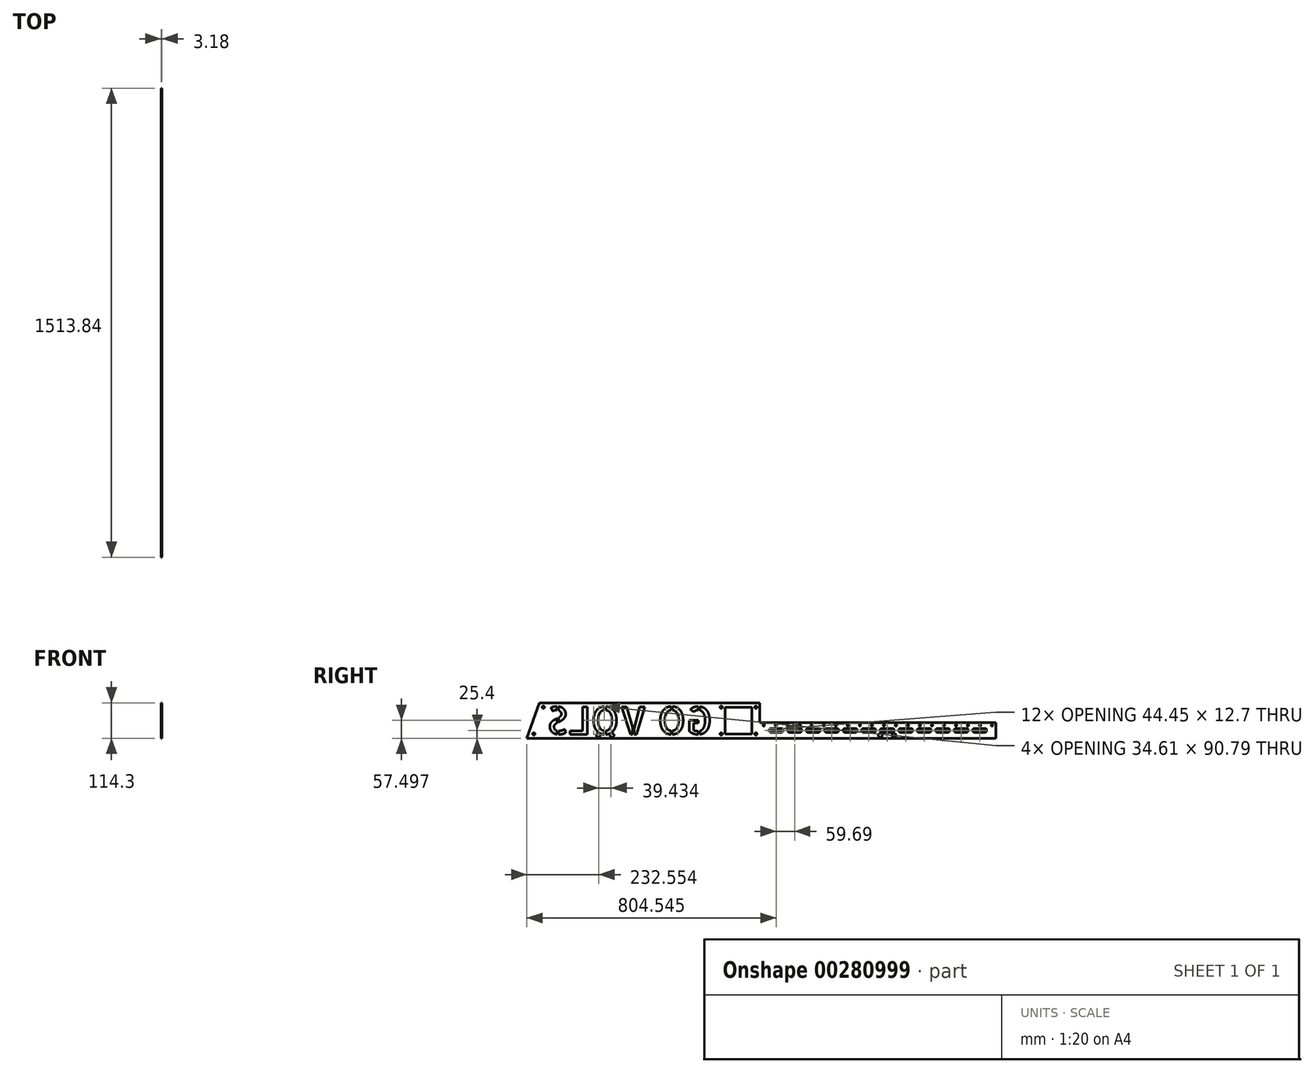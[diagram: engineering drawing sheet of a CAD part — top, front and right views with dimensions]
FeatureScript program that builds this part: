
annotation { "Feature Type Name" : "Feature", "Feature Type Description" : "" }
export const myFeature = defineFeature(function(context is Context, id is Id, definition is map)
    precondition{}
    {
        {
            var Q0;
            Q0=qCreatedBy(makeId("Right.planeOp"),FACE);
            var sketch = newSketch(context, id + "F0", { "sketchPlane" : qUnion([Q0])});
            skLineSegment(sketch, "E0", {"start": v(0, 0) * mm, "end": v(40.64, 114.3) * mm});
            skLineSegment(sketch, "E1", {"start": v(40.64, 114.3) * mm, "end": v(751.84, 114.3) * mm});
            skLineSegment(sketch, "E2", {"start": v(751.84, 114.3) * mm, "end": v(751.84, 50.8) * mm});
            skLineSegment(sketch, "E3", {"start": v(751.84, 50.8) * mm, "end": v(1513.84, 50.8) * mm});
            skLineSegment(sketch, "E4", {"start": v(1513.84, 50.8) * mm, "end": v(1513.84, 0) * mm});
            skLineSegment(sketch, "E5", {"start": v(1513.84, 0) * mm, "end": v(0, 0) * mm});
            skSolve(sketch);
        }
        {
            var Q0;
            Q0=qSketchRegion(id+"F0",true);
            extrude(context, id + "F1", {"entities" : qUnion([Q0]), "oppositeDirection" : true, "depth" : 3.17 * mm});
        }
        {
            var Q0;
            Q0=makeQuery(id+"F1.opExtrude","CAP_FACE",FACE,{"disambiguationData":[OSD([sQuery(id+"F0.wireOp",EDGE,"E0"),sQuery(id+"F0.wireOp",EDGE,"E1"),sQuery(id+"F0.wireOp",EDGE,"E2"),sQuery(id+"F0.wireOp",EDGE,"E3"),sQuery(id+"F0.wireOp",EDGE,"E4"),sQuery(id+"F0.wireOp",EDGE,"E5")])],"isStart":true});
            var sketch = newSketch(context, id + "F2", { "sketchPlane" : qUnion([Q0])});
            skLineSegment(sketch, "E6.bottom", {"start": v(726.44, 13.97) * mm, "end": v(640.08, 13.97) * mm});
            skLineSegment(sketch, "E6.top", {"start": v(726.44, 100.33) * mm, "end": v(640.08, 100.33) * mm});
            skLineSegment(sketch, "E6.left", {"start": v(726.44, 13.97) * mm, "end": v(726.44, 100.33) * mm});
            skLineSegment(sketch, "E6.right", {"start": v(640.08, 13.97) * mm, "end": v(640.08, 100.33) * mm});
            skPoint(sketch, "E6.middle", {"position": v(683.26, 57.15) * mm});
            skSolve(sketch);
        }
        {
            var Q0;
            Q0=qSketchRegion(id+"F2",true);
            var Q1;
            Q1=makeQuery(id+"F1.opExtrude","CAP_FACE",FACE,{"disambiguationData":[OSD([sQuery(id+"F0.wireOp",EDGE,"E0"),sQuery(id+"F0.wireOp",EDGE,"E1"),sQuery(id+"F0.wireOp",EDGE,"E2"),sQuery(id+"F0.wireOp",EDGE,"E3"),sQuery(id+"F0.wireOp",EDGE,"E4"),sQuery(id+"F0.wireOp",EDGE,"E5")])],"isStart":false});
            extrude(context, id + "F3", {"entities" : qUnion([Q0]), "operationType" : NewBodyOperationType.REMOVE, "endBound" : BoundingType.UP_TO_SURFACE, "oppositeDirection" : true, "endBoundEntityFace" : qUnion([Q1]), "depth" : 25.4 * mm});
        }
        {
            var Q0;
            Q0=makeQuery(id+"F1.opExtrude","CAP_FACE",FACE,{"disambiguationData":[OSD([sQuery(id+"F0.wireOp",EDGE,"E0"),sQuery(id+"F0.wireOp",EDGE,"E1"),sQuery(id+"F0.wireOp",EDGE,"E2"),sQuery(id+"F0.wireOp",EDGE,"E3"),sQuery(id+"F0.wireOp",EDGE,"E4"),sQuery(id+"F0.wireOp",EDGE,"E5")])],"isStart":true});
            var sketch = newSketch(context, id + "F4", { "sketchPlane" : qUnion([Q0])});
            skLineSegment(sketch, "E7", {"start": v(683.26, 100.33) * mm, "end": v(683.26, 63.34) * mm, "construction": true});
            skPoint(sketch, "E7.endSnap0", {"position": v(683.26, 100.33) * mm});
            skLineSegment(sketch, "E8", {"start": v(640.08, 57.15) * mm, "end": v(671.5, 57.15) * mm, "construction": true});
            skLineSegment(sketch, "E9", {"start": v(640.08, 100.33) * mm, "end": v(-159.31, 100.33) * mm, "construction": true});
            skCircle(sketch, "E10", {"center": v(739.14, 100.33) * mm, "radius": 3.81 * mm});
            skCircle(sketch, "E11.MirrorC", {"center": v(627.38, 100.33) * mm, "radius": 3.81 * mm});
            skCircle(sketch, "E12.MirrorC", {"center": v(627.38, 13.97) * mm, "radius": 3.81 * mm});
            skCircle(sketch, "E13.MirrorC", {"center": v(739.14, 13.97) * mm, "radius": 3.81 * mm});
            skCircle(sketch, "E14", {"center": v(53.34, 100.33) * mm, "radius": 3.81 * mm});
            skLineSegment(sketch, "E15", {"start": v(640.08, 13.97) * mm, "end": v(0, 13.97) * mm, "construction": true});
            skCircle(sketch, "E16", {"center": v(22.63, 13.97) * mm, "radius": 3.81 * mm});
            skLineSegment(sketch, "E17", {"start": v(53.34, 100.33) * mm, "end": v(8.36, -26.17) * mm, "construction": true});
            skCircle(sketch, "E18", {"center": v(230.38, 9.4) * mm, "radius": 6.35 * mm});
            skCircle(sketch, "E19", {"center": v(274.83, 9.4) * mm, "radius": 6.35 * mm});
            skLineSegment(sketch, "E20", {"start": v(274.83, 9.4) * mm, "end": v(1648.28, 9.4) * mm, "construction": true});
            skCircle(sketch, "E21", {"center": v(1140.46, 9.4) * mm, "radius": 6.35 * mm});
            skCircle(sketch, "E22", {"center": v(1184.9, 9.4) * mm, "radius": 6.35 * mm});
            skLineSegment(sketch, "E23", {"start": v(1513.84, 25.4) * mm, "end": v(751.84, 25.4) * mm, "construction": true});
            skLineSegment(sketch, "E24.bottom", {"start": v(821.7, 31.75) * mm, "end": v(787.4, 31.75) * mm});
            skLineSegment(sketch, "E24.top", {"start": v(821.7, 19.05) * mm, "end": v(787.4, 19.05) * mm});
            skLineSegment(sketch, "E24.left", {"start": v(826.77, 26.67) * mm, "end": v(826.77, 24.13) * mm});
            skLineSegment(sketch, "E24.right", {"start": v(782.32, 26.67) * mm, "end": v(782.32, 24.13) * mm});
            skPoint(sketch, "E24.middle", {"position": v(804.54, 25.4) * mm});
            skPoint(sketch, "E25.visualSharp", {"position": v(826.77, 31.75) * mm});
            skArc(sketch, "E25.filletArc", {"start": v(826.77, 26.67) * mm, "mid": v(825.28, 30.26) * mm, "end": v(821.7, 31.75) * mm});
            skPoint(sketch, "E26.visualSharp", {"position": v(782.32, 31.75) * mm});
            skArc(sketch, "E26.filletArc", {"start": v(787.4, 31.75) * mm, "mid": v(783.8, 30.26) * mm, "end": v(782.32, 26.67) * mm});
            skPoint(sketch, "E27.visualSharp", {"position": v(782.32, 19.05) * mm});
            skArc(sketch, "E27.filletArc", {"start": v(782.32, 24.13) * mm, "mid": v(783.8, 20.54) * mm, "end": v(787.4, 19.05) * mm});
            skPoint(sketch, "E28.visualSharp", {"position": v(826.77, 19.05) * mm});
            skArc(sketch, "E28.filletArc", {"start": v(821.7, 19.05) * mm, "mid": v(825.28, 20.54) * mm, "end": v(826.77, 24.13) * mm});
            skLineSegment(sketch, "E29.1.0.0", {"start": v(842, 26.67) * mm, "end": v(842, 24.13) * mm});
            skLineSegment(sketch, "E29.1.0.1", {"start": v(886.46, 26.67) * mm, "end": v(886.46, 24.13) * mm});
            skLineSegment(sketch, "E29.1.0.2", {"start": v(881.38, 31.75) * mm, "end": v(847.09, 31.75) * mm});
            skArc(sketch, "E29.1.0.3", {"start": v(842, 24.13) * mm, "mid": v(843.5, 20.54) * mm, "end": v(847.09, 19.05) * mm});
            skArc(sketch, "E29.1.0.4", {"start": v(886.46, 26.67) * mm, "mid": v(884.97, 30.26) * mm, "end": v(881.38, 31.75) * mm});
            skArc(sketch, "E29.1.0.5", {"start": v(881.38, 19.05) * mm, "mid": v(884.97, 20.54) * mm, "end": v(886.46, 24.13) * mm});
            skLineSegment(sketch, "E29.1.0.6", {"start": v(881.38, 19.05) * mm, "end": v(847.09, 19.05) * mm});
            skArc(sketch, "E29.1.0.7", {"start": v(847.09, 31.75) * mm, "mid": v(843.5, 30.26) * mm, "end": v(842, 26.67) * mm});
            skLineSegment(sketch, "E29.2.0.0", {"start": v(901.7, 26.67) * mm, "end": v(901.7, 24.13) * mm});
            skLineSegment(sketch, "E29.2.0.1", {"start": v(946.15, 26.67) * mm, "end": v(946.15, 24.13) * mm});
            skLineSegment(sketch, "E29.2.0.2", {"start": v(941.07, 31.75) * mm, "end": v(906.78, 31.75) * mm});
            skArc(sketch, "E29.2.0.3", {"start": v(901.7, 24.13) * mm, "mid": v(903.19, 20.54) * mm, "end": v(906.78, 19.05) * mm});
            skArc(sketch, "E29.2.0.4", {"start": v(946.15, 26.67) * mm, "mid": v(944.66, 30.26) * mm, "end": v(941.07, 31.75) * mm});
            skArc(sketch, "E29.2.0.5", {"start": v(941.07, 19.05) * mm, "mid": v(944.66, 20.54) * mm, "end": v(946.15, 24.13) * mm});
            skLineSegment(sketch, "E29.2.0.6", {"start": v(941.07, 19.05) * mm, "end": v(906.78, 19.05) * mm});
            skArc(sketch, "E29.2.0.7", {"start": v(906.78, 31.75) * mm, "mid": v(903.19, 30.26) * mm, "end": v(901.7, 26.67) * mm});
            skLineSegment(sketch, "E29.3.0.0", {"start": v(961.39, 26.67) * mm, "end": v(961.39, 24.13) * mm});
            skLineSegment(sketch, "E29.3.0.1", {"start": v(1005.84, 26.67) * mm, "end": v(1005.84, 24.13) * mm});
            skLineSegment(sketch, "E29.3.0.2", {"start": v(1000.76, 31.75) * mm, "end": v(966.47, 31.75) * mm});
            skArc(sketch, "E29.3.0.3", {"start": v(961.39, 24.13) * mm, "mid": v(962.88, 20.54) * mm, "end": v(966.47, 19.05) * mm});
            skArc(sketch, "E29.3.0.4", {"start": v(1005.84, 26.67) * mm, "mid": v(1004.35, 30.26) * mm, "end": v(1000.76, 31.75) * mm});
            skArc(sketch, "E29.3.0.5", {"start": v(1000.76, 19.05) * mm, "mid": v(1004.35, 20.54) * mm, "end": v(1005.84, 24.13) * mm});
            skLineSegment(sketch, "E29.3.0.6", {"start": v(1000.76, 19.05) * mm, "end": v(966.47, 19.05) * mm});
            skArc(sketch, "E29.3.0.7", {"start": v(966.47, 31.75) * mm, "mid": v(962.88, 30.26) * mm, "end": v(961.39, 26.67) * mm});
            skLineSegment(sketch, "E29.4.0.0", {"start": v(1021.08, 26.67) * mm, "end": v(1021.08, 24.13) * mm});
            skLineSegment(sketch, "E29.4.0.1", {"start": v(1065.53, 26.67) * mm, "end": v(1065.53, 24.13) * mm});
            skLineSegment(sketch, "E29.4.0.2", {"start": v(1060.45, 31.75) * mm, "end": v(1026.16, 31.75) * mm});
            skArc(sketch, "E29.4.0.3", {"start": v(1021.08, 24.13) * mm, "mid": v(1022.57, 20.54) * mm, "end": v(1026.16, 19.05) * mm});
            skArc(sketch, "E29.4.0.4", {"start": v(1065.53, 26.67) * mm, "mid": v(1064.04, 30.26) * mm, "end": v(1060.45, 31.75) * mm});
            skArc(sketch, "E29.4.0.5", {"start": v(1060.45, 19.05) * mm, "mid": v(1064.04, 20.54) * mm, "end": v(1065.53, 24.13) * mm});
            skLineSegment(sketch, "E29.4.0.6", {"start": v(1060.45, 19.05) * mm, "end": v(1026.16, 19.05) * mm});
            skArc(sketch, "E29.4.0.7", {"start": v(1026.16, 31.75) * mm, "mid": v(1022.57, 30.26) * mm, "end": v(1021.08, 26.67) * mm});
            skLineSegment(sketch, "E29.5.0.0", {"start": v(1080.77, 26.67) * mm, "end": v(1080.77, 24.13) * mm});
            skLineSegment(sketch, "E29.5.0.1", {"start": v(1125.22, 26.67) * mm, "end": v(1125.22, 24.13) * mm});
            skLineSegment(sketch, "E29.5.0.2", {"start": v(1120.14, 31.75) * mm, "end": v(1085.85, 31.75) * mm});
            skArc(sketch, "E29.5.0.3", {"start": v(1080.77, 24.13) * mm, "mid": v(1082.26, 20.54) * mm, "end": v(1085.85, 19.05) * mm});
            skArc(sketch, "E29.5.0.4", {"start": v(1125.22, 26.67) * mm, "mid": v(1123.73, 30.26) * mm, "end": v(1120.14, 31.75) * mm});
            skArc(sketch, "E29.5.0.5", {"start": v(1120.14, 19.05) * mm, "mid": v(1123.73, 20.54) * mm, "end": v(1125.22, 24.13) * mm});
            skLineSegment(sketch, "E29.5.0.6", {"start": v(1120.14, 19.05) * mm, "end": v(1085.85, 19.05) * mm});
            skArc(sketch, "E29.5.0.7", {"start": v(1085.85, 31.75) * mm, "mid": v(1082.26, 30.26) * mm, "end": v(1080.77, 26.67) * mm});
            skLineSegment(sketch, "E29.6.0.0", {"start": v(1140.46, 26.67) * mm, "end": v(1140.46, 24.13) * mm});
            skLineSegment(sketch, "E29.6.0.1", {"start": v(1184.9, 26.67) * mm, "end": v(1184.9, 24.13) * mm});
            skLineSegment(sketch, "E29.6.0.2", {"start": v(1179.83, 31.75) * mm, "end": v(1145.54, 31.75) * mm});
            skArc(sketch, "E29.6.0.3", {"start": v(1140.46, 24.13) * mm, "mid": v(1141.95, 20.54) * mm, "end": v(1145.54, 19.05) * mm});
            skArc(sketch, "E29.6.0.4", {"start": v(1184.9, 26.67) * mm, "mid": v(1183.42, 30.26) * mm, "end": v(1179.83, 31.75) * mm});
            skArc(sketch, "E29.6.0.5", {"start": v(1179.83, 19.05) * mm, "mid": v(1183.42, 20.54) * mm, "end": v(1184.9, 24.13) * mm});
            skLineSegment(sketch, "E29.6.0.6", {"start": v(1179.83, 19.05) * mm, "end": v(1145.54, 19.05) * mm});
            skArc(sketch, "E29.6.0.7", {"start": v(1145.54, 31.75) * mm, "mid": v(1141.95, 30.26) * mm, "end": v(1140.46, 26.67) * mm});
            skLineSegment(sketch, "E29.7.0.0", {"start": v(1200.15, 26.67) * mm, "end": v(1200.15, 24.13) * mm});
            skLineSegment(sketch, "E29.7.0.1", {"start": v(1244.6, 26.67) * mm, "end": v(1244.6, 24.13) * mm});
            skLineSegment(sketch, "E29.7.0.2", {"start": v(1239.52, 31.75) * mm, "end": v(1205.23, 31.75) * mm});
            skArc(sketch, "E29.7.0.3", {"start": v(1200.15, 24.13) * mm, "mid": v(1201.64, 20.54) * mm, "end": v(1205.23, 19.05) * mm});
            skArc(sketch, "E29.7.0.4", {"start": v(1244.6, 26.67) * mm, "mid": v(1243.11, 30.26) * mm, "end": v(1239.52, 31.75) * mm});
            skArc(sketch, "E29.7.0.5", {"start": v(1239.52, 19.05) * mm, "mid": v(1243.11, 20.54) * mm, "end": v(1244.6, 24.13) * mm});
            skLineSegment(sketch, "E29.7.0.6", {"start": v(1239.52, 19.05) * mm, "end": v(1205.23, 19.05) * mm});
            skArc(sketch, "E29.7.0.7", {"start": v(1205.23, 31.75) * mm, "mid": v(1201.64, 30.26) * mm, "end": v(1200.15, 26.67) * mm});
            skLineSegment(sketch, "E29.8.0.0", {"start": v(1259.84, 26.67) * mm, "end": v(1259.84, 24.13) * mm});
            skLineSegment(sketch, "E29.8.0.1", {"start": v(1304.29, 26.67) * mm, "end": v(1304.29, 24.13) * mm});
            skLineSegment(sketch, "E29.8.0.2", {"start": v(1299.2, 31.75) * mm, "end": v(1264.92, 31.75) * mm});
            skArc(sketch, "E29.8.0.3", {"start": v(1259.84, 24.13) * mm, "mid": v(1261.33, 20.54) * mm, "end": v(1264.92, 19.05) * mm});
            skArc(sketch, "E29.8.0.4", {"start": v(1304.29, 26.67) * mm, "mid": v(1302.8, 30.26) * mm, "end": v(1299.2, 31.75) * mm});
            skArc(sketch, "E29.8.0.5", {"start": v(1299.2, 19.05) * mm, "mid": v(1302.8, 20.54) * mm, "end": v(1304.29, 24.13) * mm});
            skLineSegment(sketch, "E29.8.0.6", {"start": v(1299.2, 19.05) * mm, "end": v(1264.92, 19.05) * mm});
            skArc(sketch, "E29.8.0.7", {"start": v(1264.92, 31.75) * mm, "mid": v(1261.33, 30.26) * mm, "end": v(1259.84, 26.67) * mm});
            skLineSegment(sketch, "E29.9.0.0", {"start": v(1319.53, 26.67) * mm, "end": v(1319.53, 24.13) * mm});
            skLineSegment(sketch, "E29.9.0.1", {"start": v(1363.98, 26.67) * mm, "end": v(1363.98, 24.13) * mm});
            skLineSegment(sketch, "E29.9.0.2", {"start": v(1358.9, 31.75) * mm, "end": v(1324.6, 31.75) * mm});
            skArc(sketch, "E29.9.0.3", {"start": v(1319.53, 24.13) * mm, "mid": v(1321.02, 20.54) * mm, "end": v(1324.6, 19.05) * mm});
            skArc(sketch, "E29.9.0.4", {"start": v(1363.98, 26.67) * mm, "mid": v(1362.5, 30.26) * mm, "end": v(1358.9, 31.75) * mm});
            skArc(sketch, "E29.9.0.5", {"start": v(1358.9, 19.05) * mm, "mid": v(1362.5, 20.54) * mm, "end": v(1363.98, 24.13) * mm});
            skLineSegment(sketch, "E29.9.0.6", {"start": v(1358.9, 19.05) * mm, "end": v(1324.6, 19.05) * mm});
            skArc(sketch, "E29.9.0.7", {"start": v(1324.6, 31.75) * mm, "mid": v(1321.02, 30.26) * mm, "end": v(1319.53, 26.67) * mm});
            skLineSegment(sketch, "E29.10.0.0", {"start": v(1379.22, 26.67) * mm, "end": v(1379.22, 24.13) * mm});
            skLineSegment(sketch, "E29.10.0.1", {"start": v(1423.67, 26.67) * mm, "end": v(1423.67, 24.13) * mm});
            skLineSegment(sketch, "E29.10.0.2", {"start": v(1418.59, 31.75) * mm, "end": v(1384.3, 31.75) * mm});
            skArc(sketch, "E29.10.0.3", {"start": v(1379.22, 24.13) * mm, "mid": v(1380.7, 20.54) * mm, "end": v(1384.3, 19.05) * mm});
            skArc(sketch, "E29.10.0.4", {"start": v(1423.67, 26.67) * mm, "mid": v(1422.18, 30.26) * mm, "end": v(1418.59, 31.75) * mm});
            skArc(sketch, "E29.10.0.5", {"start": v(1418.59, 19.05) * mm, "mid": v(1422.18, 20.54) * mm, "end": v(1423.67, 24.13) * mm});
            skLineSegment(sketch, "E29.10.0.6", {"start": v(1418.59, 19.05) * mm, "end": v(1384.3, 19.05) * mm});
            skArc(sketch, "E29.10.0.7", {"start": v(1384.3, 31.75) * mm, "mid": v(1380.7, 30.26) * mm, "end": v(1379.22, 26.67) * mm});
            skLineSegment(sketch, "E29.11.0.0", {"start": v(1438.9, 26.67) * mm, "end": v(1438.9, 24.13) * mm});
            skLineSegment(sketch, "E29.11.0.1", {"start": v(1483.36, 26.67) * mm, "end": v(1483.36, 24.13) * mm});
            skLineSegment(sketch, "E29.11.0.2", {"start": v(1478.28, 31.75) * mm, "end": v(1443.99, 31.75) * mm});
            skArc(sketch, "E29.11.0.3", {"start": v(1438.9, 24.13) * mm, "mid": v(1440.4, 20.54) * mm, "end": v(1443.99, 19.05) * mm});
            skArc(sketch, "E29.11.0.4", {"start": v(1483.36, 26.67) * mm, "mid": v(1481.87, 30.26) * mm, "end": v(1478.28, 31.75) * mm});
            skArc(sketch, "E29.11.0.5", {"start": v(1478.28, 19.05) * mm, "mid": v(1481.87, 20.54) * mm, "end": v(1483.36, 24.13) * mm});
            skLineSegment(sketch, "E29.11.0.6", {"start": v(1478.28, 19.05) * mm, "end": v(1443.99, 19.05) * mm});
            skArc(sketch, "E29.11.0.7", {"start": v(1443.99, 31.75) * mm, "mid": v(1440.4, 30.26) * mm, "end": v(1438.9, 26.67) * mm});
            skLineSegment(sketch, "E29.direction1", {"start": v(787.4, 31.75) * mm, "end": v(847.09, 31.75) * mm, "construction": true});
            skCircle(sketch, "E30", {"center": v(764.54, 41.91) * mm, "radius": 2.54 * mm});
            skCircle(sketch, "E31.1.0.0", {"center": v(803.3, 41.91) * mm, "radius": 2.54 * mm});
            skCircle(sketch, "E31.2.0.0", {"center": v(842.08, 41.91) * mm, "radius": 2.54 * mm});
            skCircle(sketch, "E31.3.0.0", {"center": v(880.84, 41.91) * mm, "radius": 2.54 * mm});
            skCircle(sketch, "E31.4.0.0", {"center": v(919.61, 41.91) * mm, "radius": 2.54 * mm});
            skCircle(sketch, "E31.5.0.0", {"center": v(958.38, 41.91) * mm, "radius": 2.54 * mm});
            skCircle(sketch, "E31.6.0.0", {"center": v(997.15, 41.91) * mm, "radius": 2.54 * mm});
            skCircle(sketch, "E31.7.0.0", {"center": v(1035.92, 41.91) * mm, "radius": 2.54 * mm});
            skCircle(sketch, "E31.8.0.0", {"center": v(1074.69, 41.91) * mm, "radius": 2.54 * mm});
            skCircle(sketch, "E31.9.0.0", {"center": v(1113.45, 41.91) * mm, "radius": 2.54 * mm});
            skCircle(sketch, "E31.10.0.0", {"center": v(1152.22, 41.91) * mm, "radius": 2.54 * mm});
            skCircle(sketch, "E31.11.0.0", {"center": v(1191, 41.91) * mm, "radius": 2.54 * mm});
            skCircle(sketch, "E31.12.0.0", {"center": v(1229.76, 41.91) * mm, "radius": 2.54 * mm});
            skCircle(sketch, "E31.13.0.0", {"center": v(1268.53, 41.91) * mm, "radius": 2.54 * mm});
            skCircle(sketch, "E31.14.0.0", {"center": v(1307.3, 41.91) * mm, "radius": 2.54 * mm});
            skCircle(sketch, "E31.15.0.0", {"center": v(1346.06, 41.91) * mm, "radius": 2.54 * mm});
            skCircle(sketch, "E31.16.0.0", {"center": v(1384.83, 41.91) * mm, "radius": 2.54 * mm});
            skCircle(sketch, "E31.17.0.0", {"center": v(1423.6, 41.91) * mm, "radius": 2.54 * mm});
            skCircle(sketch, "E31.18.0.0", {"center": v(1462.37, 41.91) * mm, "radius": 2.54 * mm});
            skCircle(sketch, "E31.19.0.0", {"center": v(1501.14, 41.91) * mm, "radius": 2.54 * mm});
            skLineSegment(sketch, "E31.direction1", {"start": v(764.54, 41.91) * mm, "end": v(803.3, 41.91) * mm, "construction": true});
            skSolve(sketch);
        }
        {
            var Q0;
            Q0=qSketchRegion(id+"F4",true);
            var Q1;
            Q1=makeQuery(id+"F1.opExtrude","CAP_FACE",FACE,{"disambiguationData":[OSD([sQuery(id+"F0.wireOp",EDGE,"E0"),sQuery(id+"F0.wireOp",EDGE,"E1"),sQuery(id+"F0.wireOp",EDGE,"E2"),sQuery(id+"F0.wireOp",EDGE,"E3"),sQuery(id+"F0.wireOp",EDGE,"E4"),sQuery(id+"F0.wireOp",EDGE,"E5")])],"isStart":false});
            extrude(context, id + "F5", {"entities" : qUnion([Q0]), "operationType" : NewBodyOperationType.REMOVE, "endBound" : BoundingType.UP_TO_SURFACE, "oppositeDirection" : true, "endBoundEntityFace" : qUnion([Q1]), "depth" : 25.4 * mm});
        }
        {
            var Q0;
            Q0=makeQuery(id+"F1.opExtrude","CAP_FACE",FACE,{"disambiguationData":[OSD([sQuery(id+"F0.wireOp",EDGE,"E0"),sQuery(id+"F0.wireOp",EDGE,"E1"),sQuery(id+"F0.wireOp",EDGE,"E2"),sQuery(id+"F0.wireOp",EDGE,"E3"),sQuery(id+"F0.wireOp",EDGE,"E4"),sQuery(id+"F0.wireOp",EDGE,"E5")])],"isStart":true});
            var sketch = newSketch(context, id + "F6", { "sketchPlane" : qUnion([Q0])});
            skLineSegment(sketch, "E32", {"start": v(65.92, 101.6) * mm, "end": v(599.44, 101.6) * mm, "construction": true});
            skLineSegment(sketch, "E33", {"start": v(599.44, 101.6) * mm, "end": v(599.44, 12.7) * mm, "construction": true});
            skLineSegment(sketch, "E34", {"start": v(599.44, 12.7) * mm, "end": v(65.92, 12.7) * mm, "construction": true});
            skLineSegment(sketch, "E35", {"start": v(65.92, 12.7) * mm, "end": v(65.92, 101.6) * mm, "construction": true});
            skSolve(sketch);
        }
        {
            var Q0;
            Q0=makeQuery(id+"F1.opExtrude","CAP_FACE",FACE,{"disambiguationData":[OSD([sQuery(id+"F0.wireOp",EDGE,"E0"),sQuery(id+"F0.wireOp",EDGE,"E1"),sQuery(id+"F0.wireOp",EDGE,"E2"),sQuery(id+"F0.wireOp",EDGE,"E3"),sQuery(id+"F0.wireOp",EDGE,"E4"),sQuery(id+"F0.wireOp",EDGE,"E5")])],"isStart":false});
            var sketch = newSketch(context, id + "F7", { "sketchPlane" : qUnion([Q0])});
            skText(sketch, "E36", { "text": "GO VOLS", "fontName": "AllertaStencil-Regular.ttf"});
            const initialGuessF7  = {"E36": [-0.59944, 0.0127, 1, 0, 0.0889]};
            skSetInitialGuess(sketch, initialGuessF7);
            skSolve(sketch);
        }
        {
            var Q0;
            Q0 = qSketchRegion(id + "F7", true);
            var Q1;
            Q1=makeQuery(id+"F1.opExtrude","CAP_FACE",FACE,{"disambiguationData":[OSD([sQuery(id+"F0.wireOp",EDGE,"E0"),sQuery(id+"F0.wireOp",EDGE,"E1"),sQuery(id+"F0.wireOp",EDGE,"E2"),sQuery(id+"F0.wireOp",EDGE,"E3"),sQuery(id+"F0.wireOp",EDGE,"E4"),sQuery(id+"F0.wireOp",EDGE,"E5")])],"isStart":true});
            extrude(context, id + "F8", {"entities" : qUnion([Q0]), "operationType" : NewBodyOperationType.REMOVE, "endBound" : BoundingType.UP_TO_SURFACE, "oppositeDirection" : true, "endBoundEntityFace" : qUnion([Q1]), "depth" : 25.4 * mm});
        }
    });
